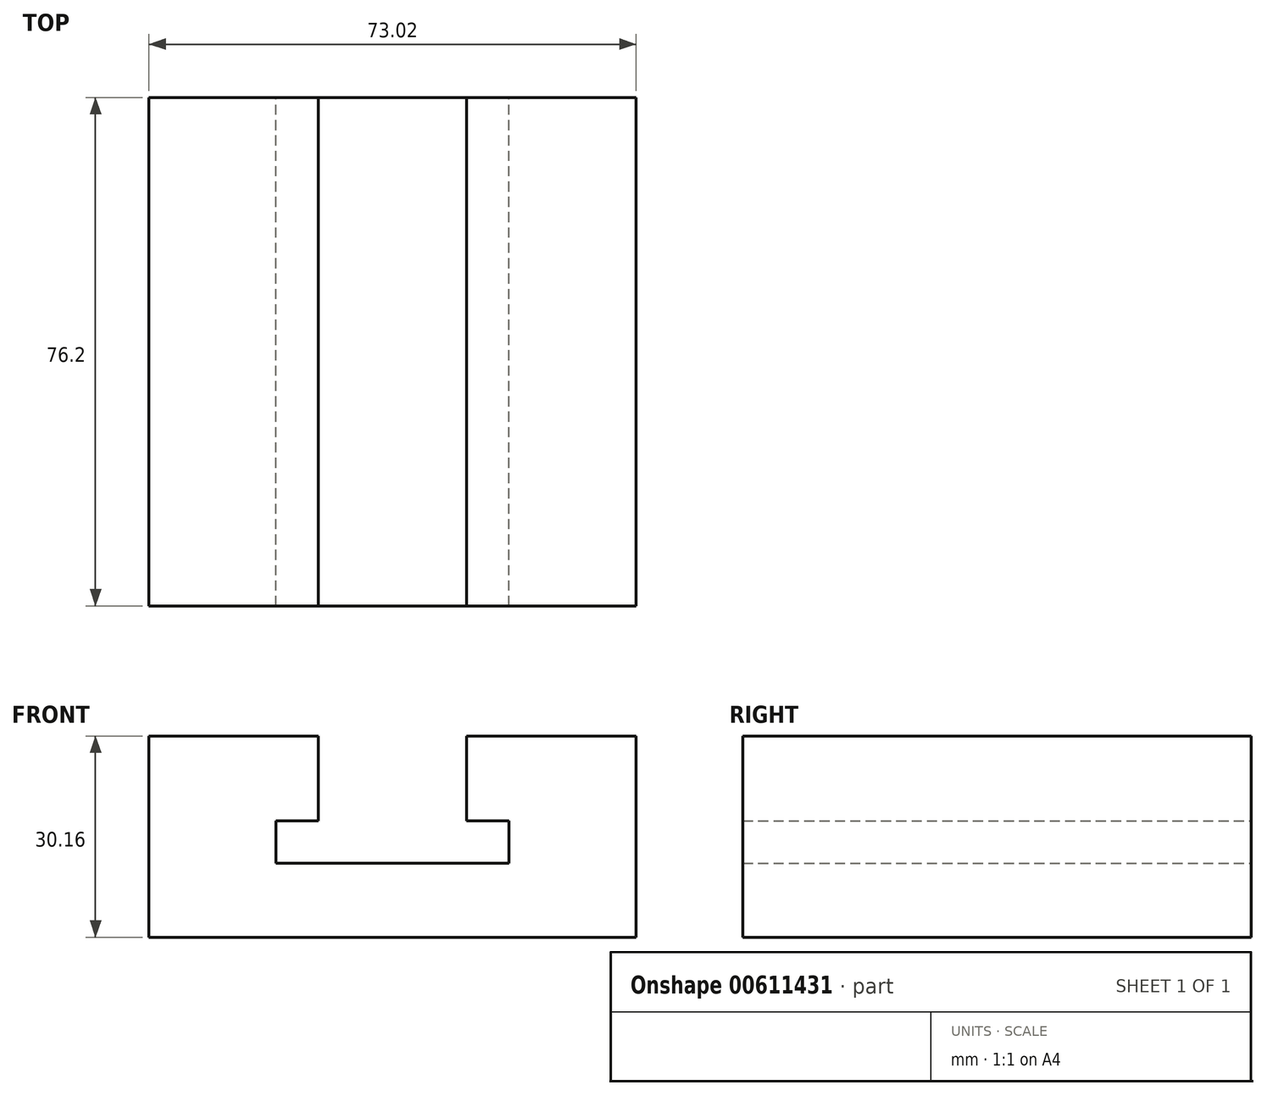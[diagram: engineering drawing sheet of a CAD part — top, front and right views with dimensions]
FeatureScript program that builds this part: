
annotation { "Feature Type Name" : "Feature", "Feature Type Description" : "" }
export const myFeature = defineFeature(function(context is Context, id is Id, definition is map)
    precondition{}
    {
        {
            var Q0;
            Q0=qCreatedBy(makeId("Front.planeOp"),FACE);
            var sketch = newSketch(context, id + "F0", { "sketchPlane" : qUnion([Q0])});
            skLineSegment(sketch, "E0", {"start": v(0, 0) * mm, "end": v(-25.4, 0) * mm});
            skLineSegment(sketch, "E1", {"start": v(-25.4, 0) * mm, "end": v(-25.4, -30.16) * mm});
            skLineSegment(sketch, "E2", {"start": v(-25.4, -30.16) * mm, "end": v(47.62, -30.16) * mm});
            skLineSegment(sketch, "E3", {"start": v(47.62, -30.16) * mm, "end": v(47.62, 0) * mm});
            skLineSegment(sketch, "E4", {"start": v(47.62, 0) * mm, "end": v(22.23, 0) * mm});
            skLineSegment(sketch, "E5", {"start": v(22.23, 0) * mm, "end": v(22.23, -12.7) * mm});
            skLineSegment(sketch, "E6", {"start": v(22.23, -12.7) * mm, "end": v(28.58, -12.7) * mm});
            skLineSegment(sketch, "E7", {"start": v(28.58, -12.7) * mm, "end": v(28.58, -19.05) * mm});
            skLineSegment(sketch, "E8", {"start": v(0, 0) * mm, "end": v(0, -12.7) * mm});
            skLineSegment(sketch, "E9", {"start": v(0, -12.7) * mm, "end": v(-6.35, -12.7) * mm});
            skLineSegment(sketch, "E10", {"start": v(-6.35, -12.7) * mm, "end": v(-6.35, -19.05) * mm});
            skLineSegment(sketch, "E11", {"start": v(-6.35, -19.05) * mm, "end": v(28.58, -19.05) * mm});
            skSolve(sketch);
        }
        {
            var Q0;
            Q0=makeQuery(id+"F0.imprint","IMPRINT",FACE,{"disambiguationData":[TD([[makeQuery(id+"F0.imprint","IMPRINT",EDGE,{"derivedFrom":sQuery(id+"F0.wireOp",EDGE,"E0")}),1.0]])]});
            extrude(context, id + "F1", {"entities" : qUnion([Q0]), "depth" : 76.2 * mm, "offsetDistance" : 25.4 * mm});
        }
    });
